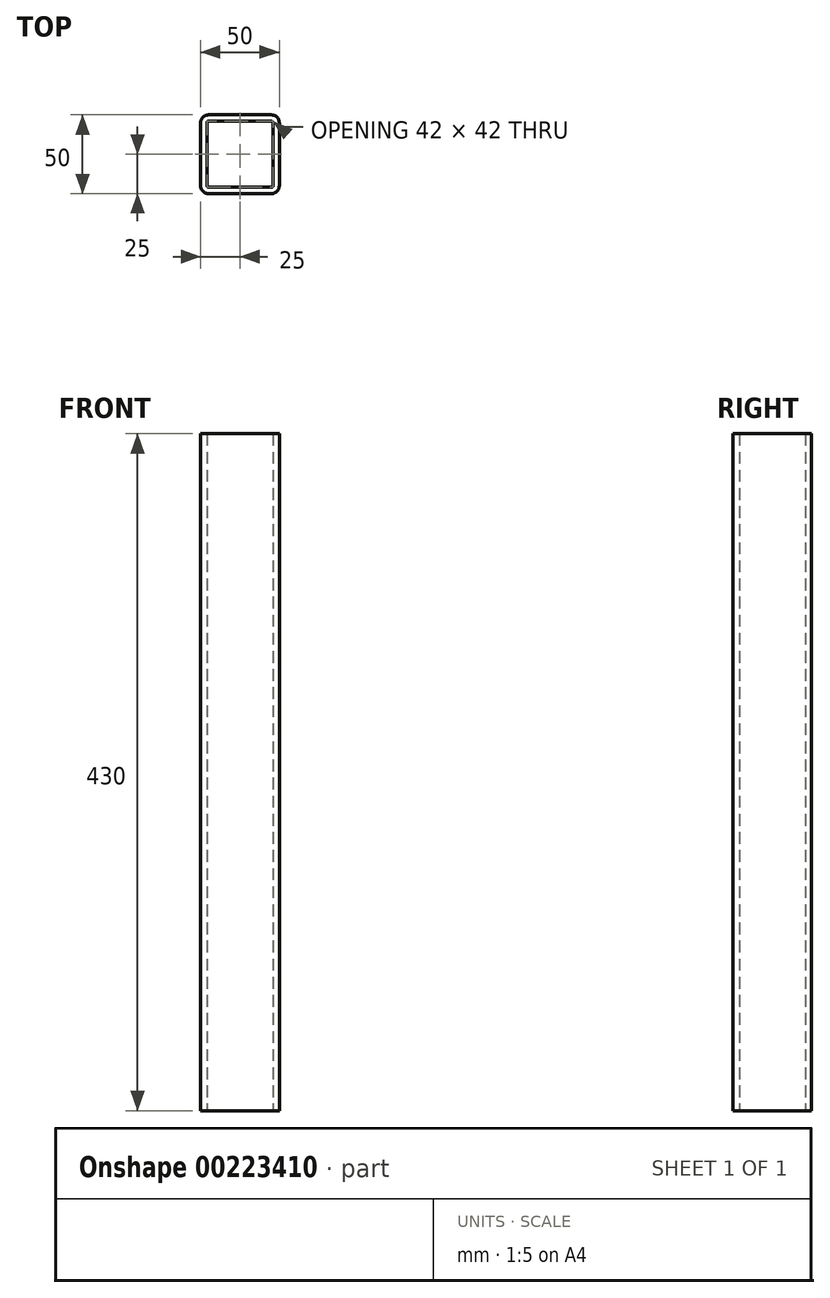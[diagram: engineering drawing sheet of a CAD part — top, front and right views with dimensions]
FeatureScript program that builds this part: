
annotation { "Feature Type Name" : "Feature", "Feature Type Description" : "" }
export const myFeature = defineFeature(function(context is Context, id is Id, definition is map)
    precondition{}
    {
        {
            var Q0;
            Q0=qCreatedBy(makeId("Top.planeOp"),FACE);
            var sketch = newSketch(context, id + "F0", { "sketchPlane" : qUnion([Q0])});
            skLineSegment(sketch, "E0.bottom", {"start": v(5, 0) * mm, "end": v(45, 0) * mm});
            skLineSegment(sketch, "E0.top", {"start": v(5, 50) * mm, "end": v(45, 50) * mm});
            skLineSegment(sketch, "E0.left", {"start": v(0, 5) * mm, "end": v(0, 45) * mm});
            skLineSegment(sketch, "E0.right", {"start": v(50, 5) * mm, "end": v(50, 45) * mm});
            skPoint(sketch, "E1.visualSharp", {"position": v(50, 50) * mm});
            skArc(sketch, "E1.filletArc", {"start": v(50, 45) * mm, "mid": v(48.54, 48.54) * mm, "end": v(45, 50) * mm});
            skPoint(sketch, "E2.visualSharp", {"position": v(50, 0) * mm});
            skArc(sketch, "E2.filletArc", {"start": v(45, 0) * mm, "mid": v(48.54, 1.46) * mm, "end": v(50, 5) * mm});
            skPoint(sketch, "E3.visualSharp", {"position": v(0, 0) * mm});
            skArc(sketch, "E3.filletArc", {"start": v(0, 5) * mm, "mid": v(1.46, 1.46) * mm, "end": v(5, 0) * mm});
            skPoint(sketch, "E4.visualSharp", {"position": v(0, 50) * mm});
            skArc(sketch, "E4.filletArc", {"start": v(5, 50) * mm, "mid": v(1.46, 48.54) * mm, "end": v(0, 45) * mm});
            skLineSegment(sketch, "E5.0", {"start": v(5, 4) * mm, "end": v(45, 4) * mm});
            skArc(sketch, "E5.1", {"start": v(4, 5) * mm, "mid": v(4.3, 4.3) * mm, "end": v(5, 4) * mm});
            skArc(sketch, "E5.2", {"start": v(45, 4) * mm, "mid": v(45.7, 4.3) * mm, "end": v(46, 5) * mm});
            skLineSegment(sketch, "E5.3", {"start": v(4, 5) * mm, "end": v(4, 45) * mm});
            skLineSegment(sketch, "E5.4", {"start": v(46, 5) * mm, "end": v(46, 45) * mm});
            skArc(sketch, "E5.5", {"start": v(46, 45) * mm, "mid": v(45.7, 45.7) * mm, "end": v(45, 46) * mm});
            skLineSegment(sketch, "E5.6", {"start": v(5, 46) * mm, "end": v(45, 46) * mm});
            skArc(sketch, "E5.7", {"start": v(5, 46) * mm, "mid": v(4.3, 45.7) * mm, "end": v(4, 45) * mm});
            skSolve(sketch);
        }
        {
            var Q0;
            Q0=makeQuery(id+"F0.imprint","IMPRINT",FACE,{"disambiguationData":[TD([[makeQuery(id+"F0.imprint","IMPRINT",EDGE,{"derivedFrom":sQuery(id+"F0.wireOp",EDGE,"E0.bottom")}),1.0]])]});
            extrude(context, id + "F1", {"entities" : qUnion([Q0]), "depth" : 430 * mm});
        }
    });
